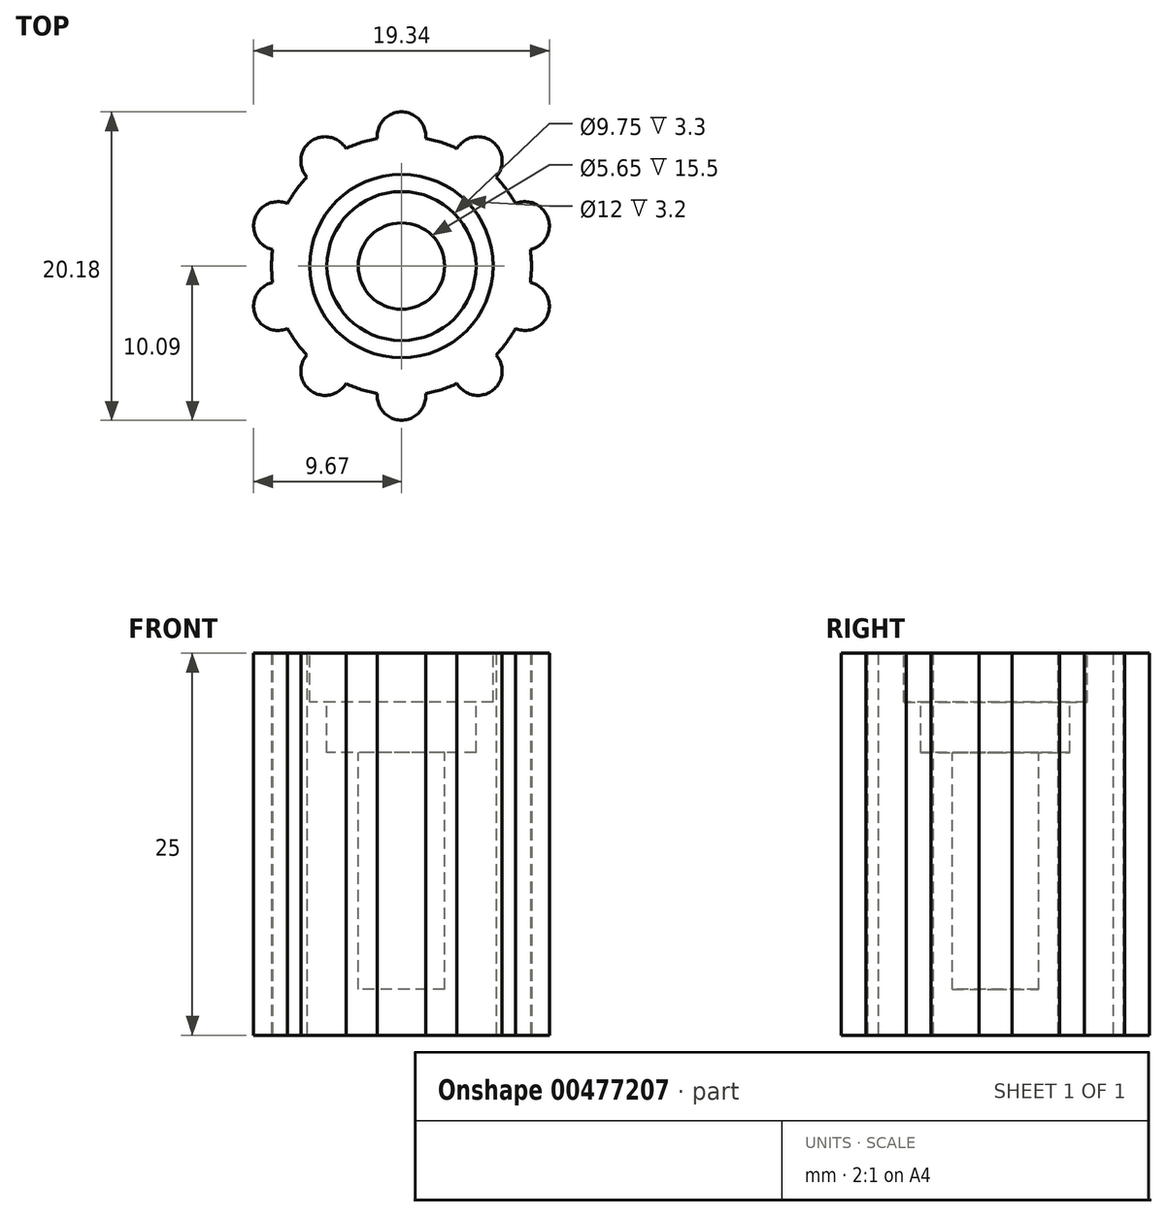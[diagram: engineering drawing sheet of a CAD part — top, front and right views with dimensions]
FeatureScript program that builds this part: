
annotation { "Feature Type Name" : "Feature", "Feature Type Description" : "" }
export const myFeature = defineFeature(function(context is Context, id is Id, definition is map)
    precondition{}
    {
        {
            var Q0;
            Q0=qCreatedBy(makeId("Top.planeOp"),FACE);
            var sketch = newSketch(context, id + "F0", { "sketchPlane" : qUnion([Q0])});
            skCircle(sketch, "E0", {"center": v(0, 0) * mm, "radius": 8.5 * mm});
            skSolve(sketch);
        }
        {
            var Q0;
            Q0=makeQuery(id+"F0.imprint","IMPRINT",FACE,{"disambiguationData":[TD([[makeQuery(id+"F0.imprint","IMPRINT",EDGE,{"derivedFrom":sQuery(id+"F0.wireOp",EDGE,"E0")}),1.0]])]});
            extrude(context, id + "F1", {"entities" : qUnion([Q0]), "depth" : 25 * mm});
        }
        {
            var Q0;
            Q0=makeQuery(id+"F1.opExtrude","CAP_FACE",FACE,{"disambiguationData":[OSD([sQuery(id+"F0.wireOp",EDGE,"E0")])],"isStart":false});
            var sketch = newSketch(context, id + "F2", { "sketchPlane" : qUnion([Q0])});
            skCircle(sketch, "E1", {"center": v(0, 0) * mm, "radius": 2.83 * mm});
            skSolve(sketch);
        }
        {
            var Q0;
            Q0 = qSketchRegion(id + "F2", true);
            extrude(context, id + "F3", {"entities" : qUnion([Q0]), "operationType" : NewBodyOperationType.REMOVE, "oppositeDirection" : true, "depth" : 22 * mm});
        }
        {
            var Q0;
            Q0=makeQuery(id+"F1.opExtrude","CAP_FACE",FACE,{"disambiguationData":[OSD([sQuery(id+"F0.wireOp",EDGE,"E0")])],"isStart":false});
            var sketch = newSketch(context, id + "F4", { "sketchPlane" : qUnion([Q0])});
            skCircle(sketch, "E2", {"center": v(0, 0) * mm, "radius": 4.88 * mm});
            skSolve(sketch);
        }
        {
            var Q0;
            Q0=makeQuery(id+"F4.imprint","IMPRINT",FACE,{"disambiguationData":[TD([[makeQuery(id+"F4.imprint","IMPRINT",EDGE,{"derivedFrom":sQuery(id+"F4.wireOp",EDGE,"E2")}),1.0]])]});
            extrude(context, id + "F5", {"entities" : qUnion([Q0]), "operationType" : NewBodyOperationType.REMOVE, "oppositeDirection" : true, "depth" : 6.5 * mm});
        }
        {
            var Q0;
            Q0=makeQuery(id+"F1.opExtrude","CAP_FACE",FACE,{"disambiguationData":[OSD([sQuery(id+"F0.wireOp",EDGE,"E0")])],"isStart":false});
            var sketch = newSketch(context, id + "F6", { "sketchPlane" : qUnion([Q0])});
            skCircle(sketch, "E3", {"center": v(0, 0) * mm, "radius": 6 * mm});
            skSolve(sketch);
        }
        {
            var Q0;
            Q0=makeQuery(id+"F6.imprint","IMPRINT",FACE,{"disambiguationData":[TD([[makeQuery(id+"F6.imprint","IMPRINT",EDGE,{"derivedFrom":sQuery(id+"F6.wireOp",EDGE,"E3")}),1.0]])]});
            extrude(context, id + "F7", {"entities" : qUnion([Q0]), "operationType" : NewBodyOperationType.REMOVE, "oppositeDirection" : true, "depth" : 3.2 * mm});
        }
        {
            var Q0;
            Q0=qCreatedBy(makeId("Top.planeOp"),FACE);
            var sketch = newSketch(context, id + "F8", { "sketchPlane" : qUnion([Q0])});
            skCircle(sketch, "E4", {"center": v(0, -8.5) * mm, "radius": 1.59 * mm});
            skCircle(sketch, "E5.1.0", {"center": v(5, -6.88) * mm, "radius": 1.59 * mm});
            skCircle(sketch, "E5.2.0", {"center": v(8.08, -2.63) * mm, "radius": 1.59 * mm});
            skCircle(sketch, "E5.3.0", {"center": v(8.08, 2.63) * mm, "radius": 1.59 * mm});
            skCircle(sketch, "E5.4.0", {"center": v(5, 6.88) * mm, "radius": 1.59 * mm});
            skCircle(sketch, "E5.5.0", {"center": v(0, 8.5) * mm, "radius": 1.59 * mm});
            skCircle(sketch, "E5.6.0", {"center": v(-5, 6.88) * mm, "radius": 1.59 * mm});
            skCircle(sketch, "E5.7.0", {"center": v(-8.08, 2.63) * mm, "radius": 1.59 * mm});
            skCircle(sketch, "E5.8.0", {"center": v(-8.08, -2.63) * mm, "radius": 1.59 * mm});
            skCircle(sketch, "E5.9.0", {"center": v(-5, -6.88) * mm, "radius": 1.59 * mm});
            skPoint(sketch, "E5.center", {"position": v(0, 0) * mm});
            skSolve(sketch);
        }
        {
            var Q0;
            Q0=makeQuery(id+"F8.imprint","IMPRINT",FACE,{"disambiguationData":[TD([[makeQuery(id+"F8.imprint","IMPRINT",EDGE,{"derivedFrom":sQuery(id+"F8.wireOp",EDGE,"E4")}),1.0]])]});
            var Q1;
            Q1=makeQuery(id+"F8.imprint","IMPRINT",FACE,{"disambiguationData":[TD([[makeQuery(id+"F8.imprint","IMPRINT",EDGE,{"derivedFrom":sQuery(id+"F8.wireOp",EDGE,"E5.1.0")}),1.0]])]});
            var Q2;
            Q2=makeQuery(id+"F8.imprint","IMPRINT",FACE,{"disambiguationData":[TD([[makeQuery(id+"F8.imprint","IMPRINT",EDGE,{"derivedFrom":sQuery(id+"F8.wireOp",EDGE,"E5.2.0")}),1.0]])]});
            var Q3;
            Q3=makeQuery(id+"F8.imprint","IMPRINT",FACE,{"disambiguationData":[TD([[makeQuery(id+"F8.imprint","IMPRINT",EDGE,{"derivedFrom":sQuery(id+"F8.wireOp",EDGE,"E5.3.0")}),1.0]])]});
            var Q4;
            Q4=makeQuery(id+"F8.imprint","IMPRINT",FACE,{"disambiguationData":[TD([[makeQuery(id+"F8.imprint","IMPRINT",EDGE,{"derivedFrom":sQuery(id+"F8.wireOp",EDGE,"E5.4.0")}),1.0]])]});
            var Q5;
            Q5=makeQuery(id+"F8.imprint","IMPRINT",FACE,{"disambiguationData":[TD([[makeQuery(id+"F8.imprint","IMPRINT",EDGE,{"derivedFrom":sQuery(id+"F8.wireOp",EDGE,"E5.5.0")}),1.0]])]});
            var Q6;
            Q6=makeQuery(id+"F8.imprint","IMPRINT",FACE,{"disambiguationData":[TD([[makeQuery(id+"F8.imprint","IMPRINT",EDGE,{"derivedFrom":sQuery(id+"F8.wireOp",EDGE,"E5.6.0")}),1.0]])]});
            var Q7;
            Q7=makeQuery(id+"F8.imprint","IMPRINT",FACE,{"disambiguationData":[TD([[makeQuery(id+"F8.imprint","IMPRINT",EDGE,{"derivedFrom":sQuery(id+"F8.wireOp",EDGE,"E5.7.0")}),1.0]])]});
            var Q8;
            Q8=makeQuery(id+"F8.imprint","IMPRINT",FACE,{"disambiguationData":[TD([[makeQuery(id+"F8.imprint","IMPRINT",EDGE,{"derivedFrom":sQuery(id+"F8.wireOp",EDGE,"E5.8.0")}),1.0]])]});
            var Q9;
            Q9=makeQuery(id+"F8.imprint","IMPRINT",FACE,{"disambiguationData":[TD([[makeQuery(id+"F8.imprint","IMPRINT",EDGE,{"derivedFrom":sQuery(id+"F8.wireOp",EDGE,"E5.9.0")}),1.0]])]});
            extrude(context, id + "F9", {"entities" : qUnion([Q0, Q1, Q2, Q3, Q4, Q5, Q6, Q7, Q8, Q9]), "operationType" : NewBodyOperationType.ADD, "depth" : 25 * mm});
        }
    });
